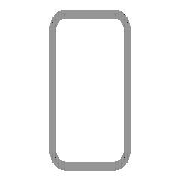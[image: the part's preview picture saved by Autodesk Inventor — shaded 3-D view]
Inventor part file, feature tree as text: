
AUTODESK INVENTOR PART (.ipt)
format: ipt  version: 2016 (Build 200138000, 138)  size: 129,024 bytes
history: native  units: mm (DEFAULTED — no unit token found)
features: other x4, sketch x3, plane x1
ambient origin geometry x8: Origin, YZ Plane, XZ Plane, XY Plane, X Axis, Y Axis, Z Axis, Center Point
bodies: Solid1 (feature_tree), Body (feature_tree)
feature tree (8):
  parser-record x1  (decoder bookkeeping rows leaked as tree rows — omitted from the tree; the rows remain in map.json)
  other  "Driven Length"
  other  "Start plane"
  other  "End plane"
  sketch  "Sketch"  dims[d7=4.0mm d9=40.0mm d11=60.0mm d12=2.0mm d13=-0.0mm d14=310.0mm d15=20.0mm d16=30.0mm d17=90.0deg d18=310.0mm]
  sketch  "Sketch3"  dims[d3=310.0mm]
  plane  "Work Plane3"
  sketch  "Sketch4"  dims[d4=0.0mm]
